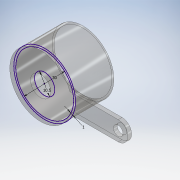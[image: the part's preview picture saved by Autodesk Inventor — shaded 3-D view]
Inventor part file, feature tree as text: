
AUTODESK INVENTOR PART (.ipt)
format: ipt  version: 2018.2 (Build 222227000, 227)  size: 135,680 bytes
history: native  units: mm
features: extrude x3, sketch x2, pattern_circular x1
ambient origin geometry x8: Origin, YZ Plane, XZ Plane, XY Plane, X Axis, Y Axis, Z Axis, Center Point
bodies: Solid1 (feature_tree)
feature tree (6):
  sketch  "Sketch1"  dims[d0=30.0mm d1=1.0mm]
  extrude  "Extrusion1"  Depth=1.0mm
  extrude  "Extrusion2"  Depth=5.0mm
  extrude  "Extrusion3"  Depth=2.0mm TaperAngle=0.0deg
  pattern_circular  "Circular Pattern1"  [2 undecoded]
  sketch  "Sketch3"  dims[d2=20.0mm d3=0.0mm d6=10.5mm d7=2.0mm d8=0.0mm d9=5.0mm d10=25.0mm d11=2.0mm d12=0.0mm d13=5.0mm d14=40.0mm d15=360.0deg]
note: 2 required parameter values undecoded (feature->parameter linkage not recoverable at this tier; creation-order binding heuristic only, values carry confidence <= 0.55)
